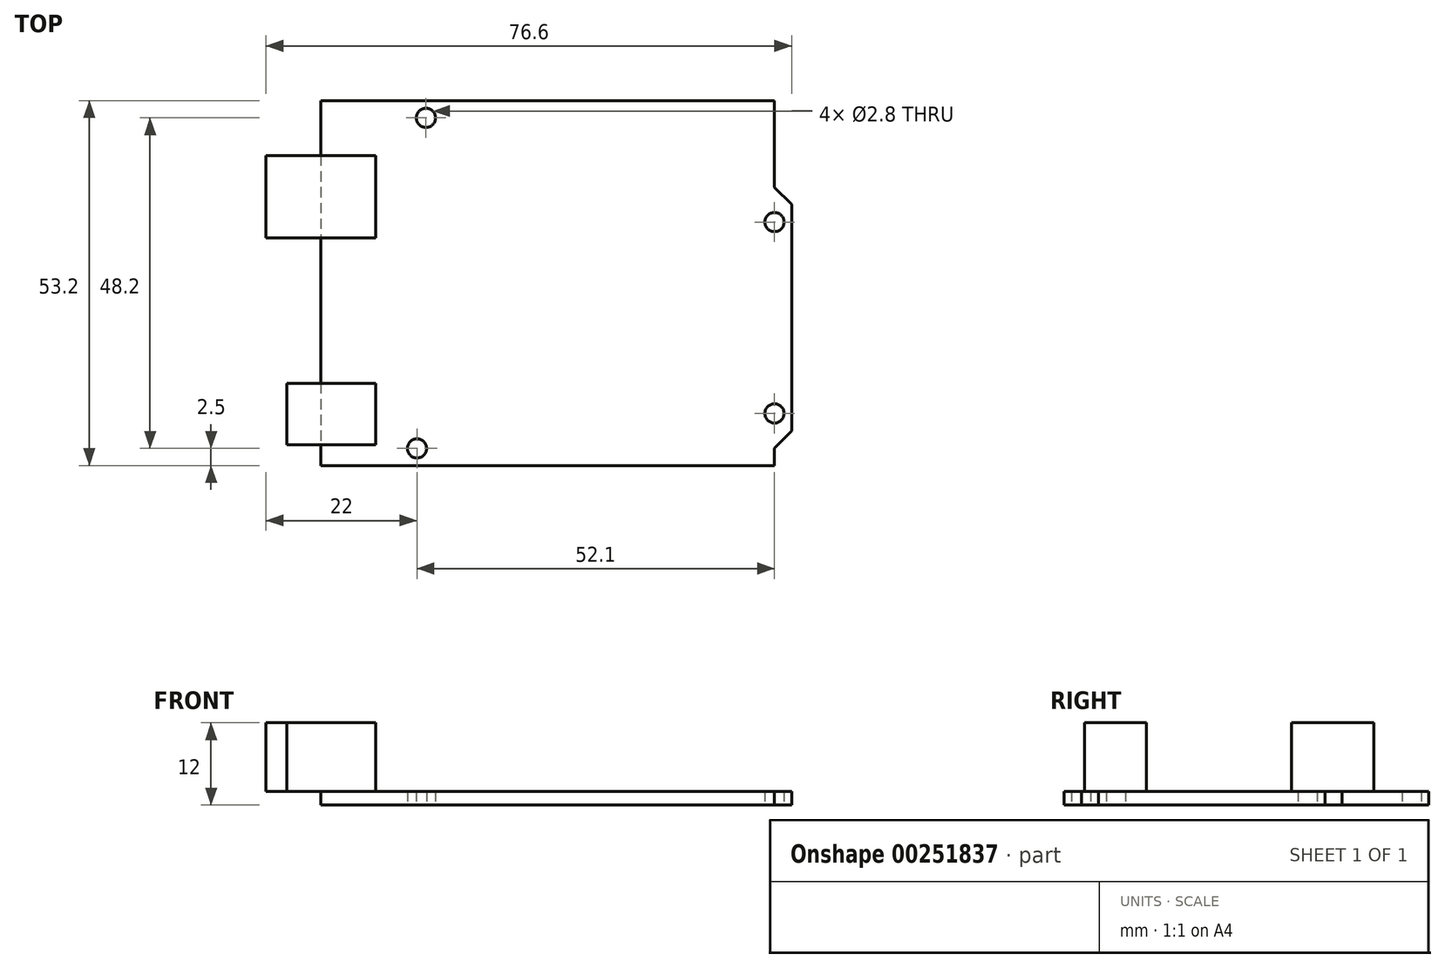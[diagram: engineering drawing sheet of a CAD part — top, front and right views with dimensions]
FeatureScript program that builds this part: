
annotation { "Feature Type Name" : "Feature", "Feature Type Description" : "" }
export const myFeature = defineFeature(function(context is Context, id is Id, definition is map)
    precondition{}
    {
        {
            var Q0;
            Q0=qCreatedBy(makeId("Top.planeOp"),FACE);
            var sketch = newSketch(context, id + "F0", { "sketchPlane" : qUnion([Q0])});
            skLineSegment(sketch, "E0", {"start": v(-10, 10) * mm, "end": v(-10, 0) * mm, "construction": true});
            skLineSegment(sketch, "E1", {"start": v(-10, 0) * mm, "end": v(-10, -10) * mm, "construction": true});
            skLineSegment(sketch, "E2", {"start": v(-10, -10) * mm, "end": v(0, -10) * mm, "construction": true});
            skLineSegment(sketch, "E3", {"start": v(0, -10) * mm, "end": v(20, -10) * mm, "construction": true});
            skLineSegment(sketch, "E4.bottom", {"start": v(20, 63.2) * mm, "end": v(86.1, 63.2) * mm});
            skLineSegment(sketch, "E4.top", {"start": v(20, 10) * mm, "end": v(86.1, 10) * mm});
            skLineSegment(sketch, "E4.left", {"start": v(20, 63.2) * mm, "end": v(20, 10) * mm});
            skLineSegment(sketch, "E5", {"start": v(35.3, -10) * mm, "end": v(86.1, -10) * mm, "construction": true});
            skLineSegment(sketch, "E6", {"start": v(-10, 12.5) * mm, "end": v(-10, 17.6) * mm, "construction": true});
            skLineSegment(sketch, "E7", {"start": v(-10, 17.6) * mm, "end": v(-10, 45.5) * mm, "construction": true});
            skCircle(sketch, "E8", {"center": v(-10, -10) * mm, "radius": 1.4 * mm, "construction": true});
            skCircle(sketch, "E9", {"center": v(34, 12.5) * mm, "radius": 1.4 * mm});
            skCircle(sketch, "E10", {"center": v(35.3, 60.7) * mm, "radius": 1.4 * mm});
            skCircle(sketch, "E11", {"center": v(86.1, 17.6) * mm, "radius": 1.4 * mm});
            skCircle(sketch, "E12", {"center": v(86.1, 45.5) * mm, "radius": 1.4 * mm});
            skLineSegment(sketch, "E13", {"start": v(-10, 45.5) * mm, "end": v(-10, 60.7) * mm, "construction": true});
            skLineSegment(sketch, "E14", {"start": v(35.3, -10) * mm, "end": v(34, -10) * mm, "construction": true});
            skLineSegment(sketch, "E15", {"start": v(34, -10) * mm, "end": v(20, -10) * mm, "construction": true});
            skLineSegment(sketch, "E16", {"start": v(86.1, -10) * mm, "end": v(88.6, -10) * mm, "construction": true});
            skLineSegment(sketch, "E17", {"start": v(-10, 60.7) * mm, "end": v(-10, 63.2) * mm, "construction": true});
            skLineSegment(sketch, "E18", {"start": v(-10, 12.5) * mm, "end": v(-10, 10) * mm, "construction": true});
            skLineSegment(sketch, "E19", {"start": v(86.1, 10) * mm, "end": v(86.1, 12.55) * mm});
            skLineSegment(sketch, "E20", {"start": v(86.1, 12.55) * mm, "end": v(88.6, 15.05) * mm});
            skLineSegment(sketch, "E21", {"start": v(88.6, 15.05) * mm, "end": v(88.6, 48.05) * mm});
            skLineSegment(sketch, "E22", {"start": v(88.6, 48.05) * mm, "end": v(86.1, 50.55) * mm});
            skLineSegment(sketch, "E23", {"start": v(86.1, 50.55) * mm, "end": v(86.1, 63.2) * mm});
            skLineSegment(sketch, "E24", {"start": v(86.1, 50.55) * mm, "end": v(86.1, 45.5) * mm, "construction": true});
            skLineSegment(sketch, "E25", {"start": v(86.1, 17.6) * mm, "end": v(86.1, 12.55) * mm, "construction": true});
            skSolve(sketch);
        }
        {
            var Q0;
            Q0=makeQuery(id+"F0.imprint","IMPRINT",FACE,{"disambiguationData":[TD([[makeQuery(id+"F0.imprint","IMPRINT",EDGE,{"derivedFrom":sQuery(id+"F0.wireOp",EDGE,"E4.bottom")}),-1.0]])]});
            extrude(context, id + "F1", {"entities" : qUnion([Q0]), "flatOperationType" : FlatOperationType.REMOVE, "offsetDistance" : 25 * mm, "depth" : 2 * mm, "domain" : OperationDomain.MODEL});
        }
        {
            var Q0;
            Q0=makeQuery(id+"F1.opExtrude","CAP_FACE",FACE,{"disambiguationData":[OSD([sQuery(id+"F0.wireOp",EDGE,"E4.bottom"),sQuery(id+"F0.wireOp",EDGE,"E4.top"),sQuery(id+"F0.wireOp",EDGE,"E4.left"),sQuery(id+"F0.wireOp",EDGE,"E9"),sQuery(id+"F0.wireOp",EDGE,"E10"),sQuery(id+"F0.wireOp",EDGE,"E11"),sQuery(id+"F0.wireOp",EDGE,"E12"),sQuery(id+"F0.wireOp",EDGE,"E19"),sQuery(id+"F0.wireOp",EDGE,"E20"),sQuery(id+"F0.wireOp",EDGE,"E21"),sQuery(id+"F0.wireOp",EDGE,"E22"),sQuery(id+"F0.wireOp",EDGE,"E23")])],"isStart":false});
            var sketch = newSketch(context, id + "F2", { "sketchPlane" : qUnion([Q0])});
            skLineSegment(sketch, "E26.bottom", {"start": v(12, 55.2) * mm, "end": v(28, 55.2) * mm});
            skLineSegment(sketch, "E26.top", {"start": v(12, 43.2) * mm, "end": v(28, 43.2) * mm});
            skLineSegment(sketch, "E26.left", {"start": v(12, 55.2) * mm, "end": v(12, 43.2) * mm});
            skLineSegment(sketch, "E26.right", {"start": v(28, 55.2) * mm, "end": v(28, 43.2) * mm});
            skLineSegment(sketch, "E27.bottom", {"start": v(15, 22) * mm, "end": v(28, 22) * mm});
            skLineSegment(sketch, "E27.top", {"start": v(15, 13) * mm, "end": v(28, 13) * mm});
            skLineSegment(sketch, "E27.left", {"start": v(15, 22) * mm, "end": v(15, 13) * mm});
            skLineSegment(sketch, "E27.right", {"start": v(28, 22) * mm, "end": v(28, 13) * mm});
            skSolve(sketch);
        }
        {
            var Q0;
            {var subQ0=sQuery(id+"F2.wireOp",EDGE,"E26.left");Q0=makeQuery(id+"F2.imprint","IMPRINT",FACE,{"disambiguationData":[TD([[makeQuery(id+"F2.imprint","IMPRINT",EDGE,{"derivedFrom":subQ0}),1.0]])]});}
            var Q1;
            {var subQ0=sQuery(id+"F2.wireOp",EDGE,"E26.right");Q1=makeQuery(id+"F2.imprint","IMPRINT",FACE,{"disambiguationData":[TD([[makeQuery(id+"F2.imprint","IMPRINT",EDGE,{"derivedFrom":subQ0}),-1.0]])]});}
            var Q2;
            {var subQ0=sQuery(id+"F2.wireOp",EDGE,"E27.left");Q2=makeQuery(id+"F2.imprint","IMPRINT",FACE,{"disambiguationData":[TD([[makeQuery(id+"F2.imprint","IMPRINT",EDGE,{"derivedFrom":subQ0}),1.0]])]});}
            var Q3;
            {var subQ0=sQuery(id+"F2.wireOp",EDGE,"E27.right");Q3=makeQuery(id+"F2.imprint","IMPRINT",FACE,{"disambiguationData":[TD([[makeQuery(id+"F2.imprint","IMPRINT",EDGE,{"derivedFrom":subQ0}),-1.0]])]});}
            extrude(context, id + "F3", {"entities" : qUnion([Q0, Q1, Q2, Q3]), "operationType" : NewBodyOperationType.ADD, "depth" : 10 * mm});
        }
    });
